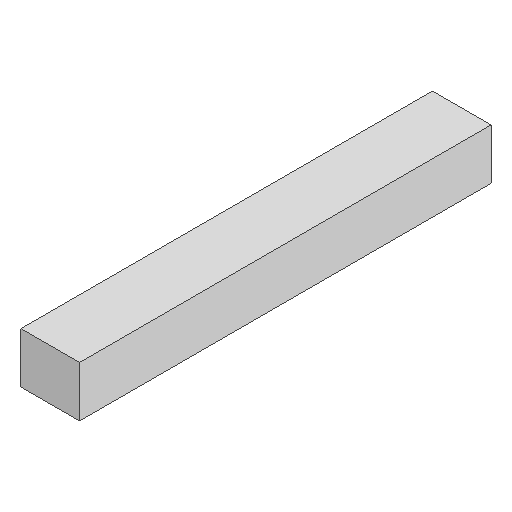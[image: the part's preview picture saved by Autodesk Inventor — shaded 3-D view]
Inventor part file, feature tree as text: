
AUTODESK INVENTOR PART (.ipt)
format: ipt  version: 2025 (Build 290162010, 162A)  size: 78,336 bytes
history: native  units: in
note: dims shown in document units (in); Inventor stores cm internally (conversion verified against a paired STEP export)
features: extrude x1, sketch x1
ambient origin geometry x8: Origin, YZ Plane, XZ Plane, XY Plane, X Axis, Y Axis, Z Axis, Center Point
bodies: Solid1 (feature_tree)
feature tree (2):
  extrude  "Extrusion1"  [1 undecoded]
  sketch  "Sketch1"  dims[d0=1.0in d1=0.0in]
note: 1 required parameter value undecoded (feature->parameter linkage not recoverable at this tier; creation-order binding heuristic only, values carry confidence <= 0.55)
